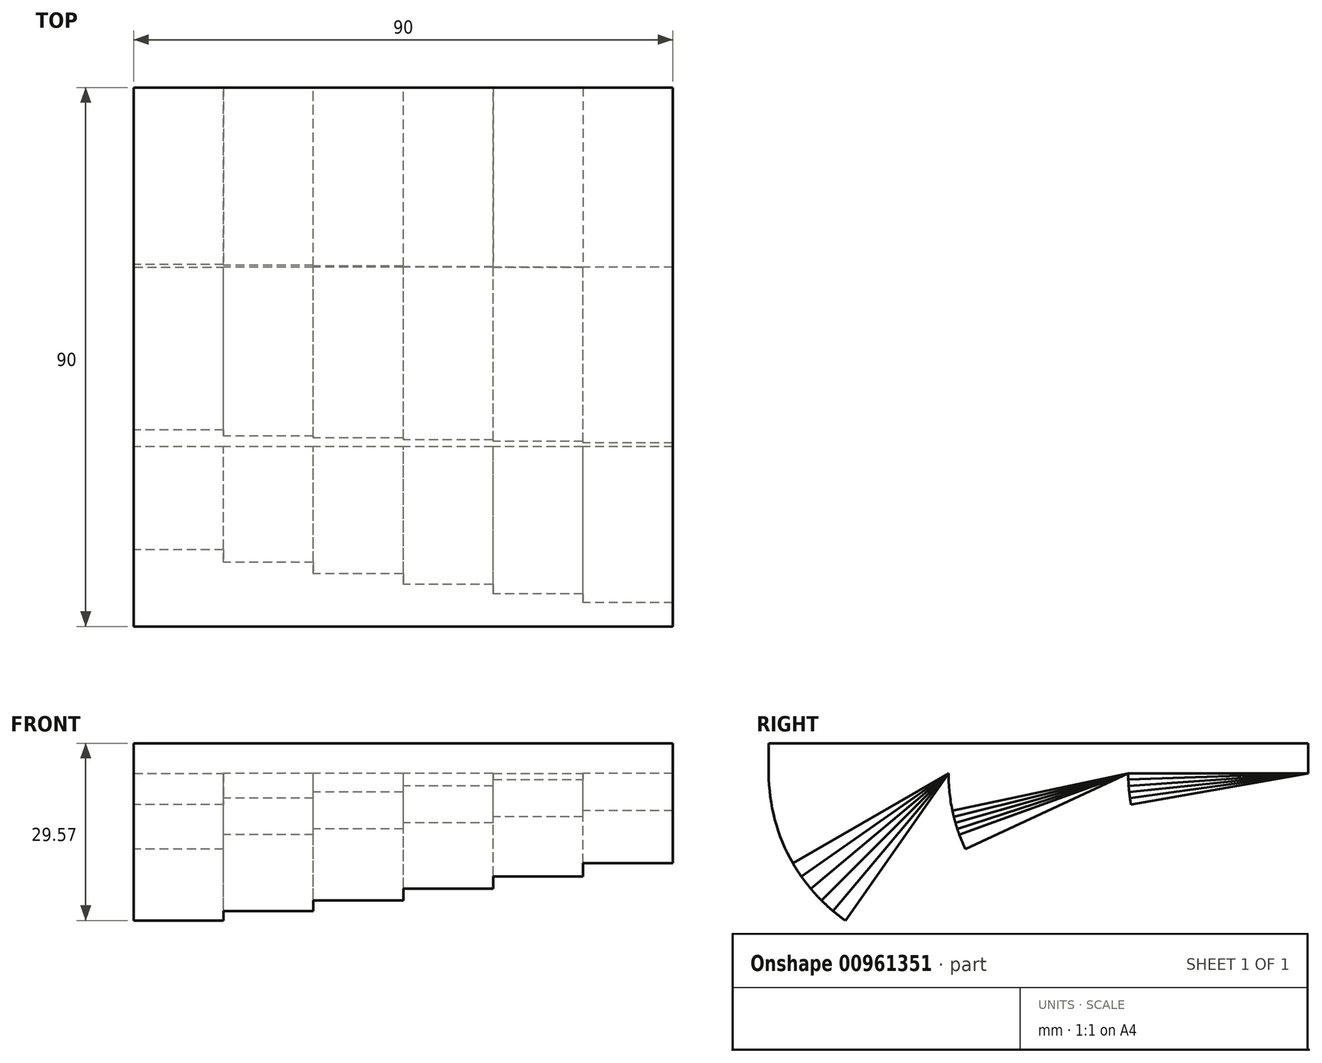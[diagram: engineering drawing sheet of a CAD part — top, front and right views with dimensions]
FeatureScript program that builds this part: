
annotation { "Feature Type Name" : "Feature", "Feature Type Description" : "" }
export const myFeature = defineFeature(function(context is Context, id is Id, definition is map)
    precondition{}
    {
        {
            var Q0;
            Q0=qCreatedBy(makeId("Top.planeOp"),FACE);
            var sketch = newSketch(context, id + "F0", { "sketchPlane" : qUnion([Q0])});
            skLineSegment(sketch, "E0.bottom", {"start": v(-45, 45) * mm, "end": v(45, 45) * mm});
            skLineSegment(sketch, "E0.top", {"start": v(-45, -45) * mm, "end": v(45, -45) * mm});
            skLineSegment(sketch, "E0.left", {"start": v(-45, -45) * mm, "end": v(-45, 45) * mm});
            skLineSegment(sketch, "E0.right", {"start": v(45, -45) * mm, "end": v(45, 45) * mm});
            skSolve(sketch);
        }
        {
            var Q0;
            Q0 = qSketchRegion(id + "F0", true);
            extrude(context, id + "F1", {"entities" : qUnion([Q0]), "depth" : 5 * mm, "offsetDistance" : 25 * mm});
        }
        {
            var Q0;
            Q0=qCreatedBy(makeId("Top.planeOp"),FACE);
            var sketch = newSketch(context, id + "F2", { "sketchPlane" : qUnion([Q0])});
            skLineSegment(sketch, "E1.bottom", {"start": v(15, 45) * mm, "end": v(30, 45) * mm});
            skLineSegment(sketch, "E1.top", {"start": v(15, 15) * mm, "end": v(30, 15) * mm});
            skLineSegment(sketch, "E1.left", {"start": v(15, 45) * mm, "end": v(15, 15) * mm});
            skLineSegment(sketch, "E1.right", {"start": v(30, 45) * mm, "end": v(30, 15) * mm});
            skSolve(sketch);
        }
        {
            var Q0;
            Q0 = qSketchRegion(id + "F2", true);
            var Q1;
            Q1=sQuery(id+"F2.wireOp",EDGE,"E1.bottom");
            revolve(context, id + "F3", {"operationType" : NewBodyOperationType.ADD, "surfaceOperationType" : NewSurfaceOperationType.NEW, "entities" : qUnion([Q0]), "axis" : qUnion([Q1]), "revolveType" : RevolveType.ONE_DIRECTION, "angle" : 2 * degree});
        }
        {
            var Q0;
            Q0=qCreatedBy(makeId("Top.planeOp"),FACE);
            var sketch = newSketch(context, id + "F4", { "sketchPlane" : qUnion([Q0])});
            skLineSegment(sketch, "E2.bottom", {"start": v(15, 15) * mm, "end": v(0, 15) * mm});
            skLineSegment(sketch, "E2.top", {"start": v(15, 45) * mm, "end": v(0, 45) * mm});
            skLineSegment(sketch, "E2.left", {"start": v(15, 15) * mm, "end": v(15, 45) * mm});
            skLineSegment(sketch, "E2.right", {"start": v(0, 15) * mm, "end": v(0, 45) * mm});
            skSolve(sketch);
        }
        {
            var Q0;
            Q0 = qSketchRegion(id + "F4", true);
            var Q1;
            Q1=sQuery(id+"F4.wireOp",EDGE,"E2.top");
            revolve(context, id + "F5", {"operationType" : NewBodyOperationType.ADD, "surfaceOperationType" : NewSurfaceOperationType.NEW, "entities" : qUnion([Q0]), "axis" : qUnion([Q1]), "revolveType" : RevolveType.ONE_DIRECTION, "oppositeDirection" : true, "angle" : 4 * degree});
        }
        {
            var Q0;
            Q0=qCreatedBy(makeId("Top.planeOp"),FACE);
            var sketch = newSketch(context, id + "F6", { "sketchPlane" : qUnion([Q0])});
            skLineSegment(sketch, "E3.bottom", {"start": v(0, 15) * mm, "end": v(-15, 15) * mm});
            skLineSegment(sketch, "E3.top", {"start": v(0, 45) * mm, "end": v(-15, 45) * mm});
            skLineSegment(sketch, "E3.left", {"start": v(0, 15) * mm, "end": v(0, 45) * mm});
            skLineSegment(sketch, "E3.right", {"start": v(-15, 15) * mm, "end": v(-15, 45) * mm});
            skSolve(sketch);
        }
        {
            var Q0;
            Q0 = qSketchRegion(id + "F6", true);
            var Q1;
            Q1=sQuery(id+"F6.wireOp",EDGE,"E3.top");
            revolve(context, id + "F7", {"operationType" : NewBodyOperationType.ADD, "surfaceOperationType" : NewSurfaceOperationType.NEW, "entities" : qUnion([Q0]), "axis" : qUnion([Q1]), "revolveType" : RevolveType.ONE_DIRECTION, "oppositeDirection" : true, "angle" : 6 * degree});
        }
        {
            var Q0;
            Q0=qCreatedBy(makeId("Top.planeOp"),FACE);
            var sketch = newSketch(context, id + "F8", { "sketchPlane" : qUnion([Q0])});
            skLineSegment(sketch, "E4.bottom", {"start": v(-15, 15) * mm, "end": v(-30, 15) * mm});
            skLineSegment(sketch, "E4.top", {"start": v(-15, 45) * mm, "end": v(-30, 45) * mm});
            skLineSegment(sketch, "E4.left", {"start": v(-15, 15) * mm, "end": v(-15, 45) * mm});
            skLineSegment(sketch, "E4.right", {"start": v(-30, 15) * mm, "end": v(-30, 45) * mm});
            skSolve(sketch);
        }
        {
            var Q0;
            Q0 = qSketchRegion(id + "F8", true);
            var Q1;
            Q1=sQuery(id+"F8.wireOp",EDGE,"E4.top");
            revolve(context, id + "F9", {"operationType" : NewBodyOperationType.ADD, "surfaceOperationType" : NewSurfaceOperationType.NEW, "entities" : qUnion([Q0]), "axis" : qUnion([Q1]), "revolveType" : RevolveType.ONE_DIRECTION, "oppositeDirection" : true, "angle" : 8 * degree});
        }
        {
            var Q0;
            Q0=qCreatedBy(makeId("Top.planeOp"),FACE);
            var sketch = newSketch(context, id + "F10", { "sketchPlane" : qUnion([Q0])});
            skLineSegment(sketch, "E5.bottom", {"start": v(-30, 45) * mm, "end": v(-45, 45) * mm});
            skLineSegment(sketch, "E5.top", {"start": v(-30, 15) * mm, "end": v(-45, 15) * mm});
            skLineSegment(sketch, "E5.left", {"start": v(-30, 45) * mm, "end": v(-30, 15) * mm});
            skLineSegment(sketch, "E5.right", {"start": v(-45, 45) * mm, "end": v(-45, 15) * mm});
            skSolve(sketch);
        }
        {
            var Q0;
            Q0 = qSketchRegion(id + "F10", true);
            var Q1;
            Q1=sQuery(id+"F10.wireOp",EDGE,"E5.bottom");
            revolve(context, id + "F11", {"operationType" : NewBodyOperationType.ADD, "surfaceOperationType" : NewSurfaceOperationType.NEW, "entities" : qUnion([Q0]), "axis" : qUnion([Q1]), "revolveType" : RevolveType.ONE_DIRECTION, "oppositeDirection" : true, "angle" : 10 * degree});
        }
        {
            var Q0;
            Q0=qCreatedBy(makeId("Top.planeOp"),FACE);
            var sketch = newSketch(context, id + "F12", { "sketchPlane" : qUnion([Q0])});
            skLineSegment(sketch, "E6.bottom", {"start": v(45, -15) * mm, "end": v(30, -15) * mm});
            skLineSegment(sketch, "E6.top", {"start": v(45, 15) * mm, "end": v(30, 15) * mm});
            skLineSegment(sketch, "E6.left", {"start": v(45, -15) * mm, "end": v(45, 15) * mm});
            skLineSegment(sketch, "E6.right", {"start": v(30, -15) * mm, "end": v(30, 15) * mm});
            skSolve(sketch);
        }
        {
            var Q0;
            Q0 = qSketchRegion(id + "F12", true);
            var Q1;
            Q1=sQuery(id+"F12.wireOp",EDGE,"E6.top");
            revolve(context, id + "F13", {"operationType" : NewBodyOperationType.ADD, "surfaceOperationType" : NewSurfaceOperationType.NEW, "entities" : qUnion([Q0]), "axis" : qUnion([Q1]), "revolveType" : RevolveType.ONE_DIRECTION, "oppositeDirection" : true, "angle" : 12 * degree});
        }
        {
            var Q0;
            Q0=qCreatedBy(makeId("Top.planeOp"),FACE);
            var sketch = newSketch(context, id + "F14", { "sketchPlane" : qUnion([Q0])});
            skLineSegment(sketch, "E7.bottom", {"start": v(30, -15) * mm, "end": v(15, -15) * mm});
            skLineSegment(sketch, "E7.top", {"start": v(30, 15) * mm, "end": v(15, 15) * mm});
            skLineSegment(sketch, "E7.left", {"start": v(30, -15) * mm, "end": v(30, 15) * mm});
            skLineSegment(sketch, "E7.right", {"start": v(15, -15) * mm, "end": v(15, 15) * mm});
            skSolve(sketch);
        }
        {
            var Q0;
            Q0 = qSketchRegion(id + "F14", true);
            var Q1;
            Q1=sQuery(id+"F14.wireOp",EDGE,"E7.top");
            revolve(context, id + "F15", {"operationType" : NewBodyOperationType.ADD, "surfaceOperationType" : NewSurfaceOperationType.NEW, "entities" : qUnion([Q0]), "axis" : qUnion([Q1]), "revolveType" : RevolveType.ONE_DIRECTION, "oppositeDirection" : true, "angle" : 14 * degree});
        }
        {
            var Q0;
            Q0=qCreatedBy(makeId("Top.planeOp"),FACE);
            var sketch = newSketch(context, id + "F16", { "sketchPlane" : qUnion([Q0])});
            skLineSegment(sketch, "E8.bottom", {"start": v(15, -15) * mm, "end": v(0, -15) * mm});
            skLineSegment(sketch, "E8.top", {"start": v(15, 15) * mm, "end": v(0, 15) * mm});
            skLineSegment(sketch, "E8.left", {"start": v(15, -15) * mm, "end": v(15, 15) * mm});
            skLineSegment(sketch, "E8.right", {"start": v(0, -15) * mm, "end": v(0, 15) * mm});
            skSolve(sketch);
        }
        {
            var Q0;
            Q0 = qSketchRegion(id + "F16", true);
            var Q1;
            Q1=sQuery(id+"F16.wireOp",EDGE,"E8.top");
            revolve(context, id + "F17", {"operationType" : NewBodyOperationType.ADD, "surfaceOperationType" : NewSurfaceOperationType.NEW, "entities" : qUnion([Q0]), "axis" : qUnion([Q1]), "revolveType" : RevolveType.ONE_DIRECTION, "oppositeDirection" : true, "angle" : 16 * degree});
        }
        {
            var Q0;
            Q0=qCreatedBy(makeId("Top.planeOp"),FACE);
            var sketch = newSketch(context, id + "F18", { "sketchPlane" : qUnion([Q0])});
            skLineSegment(sketch, "E9.bottom", {"start": v(0, -15) * mm, "end": v(-15, -15) * mm});
            skLineSegment(sketch, "E9.top", {"start": v(0, 15) * mm, "end": v(-15, 15) * mm});
            skLineSegment(sketch, "E9.left", {"start": v(0, -15) * mm, "end": v(0, 15) * mm});
            skLineSegment(sketch, "E9.right", {"start": v(-15, -15) * mm, "end": v(-15, 15) * mm});
            skSolve(sketch);
        }
        {
            var Q0;
            Q0 = qSketchRegion(id + "F18", true);
            var Q1;
            Q1=sQuery(id+"F6.wireOp",EDGE,"E3.bottom");
            revolve(context, id + "F19", {"operationType" : NewBodyOperationType.ADD, "surfaceOperationType" : NewSurfaceOperationType.NEW, "entities" : qUnion([Q0]), "axis" : qUnion([Q1]), "revolveType" : RevolveType.ONE_DIRECTION, "oppositeDirection" : true, "angle" : 18 * degree});
        }
        {
            var Q0;
            Q0=qCreatedBy(makeId("Top.planeOp"),FACE);
            var sketch = newSketch(context, id + "F20", { "sketchPlane" : qUnion([Q0])});
            skLineSegment(sketch, "E10.bottom", {"start": v(-15, -15) * mm, "end": v(-30, -15) * mm});
            skLineSegment(sketch, "E10.top", {"start": v(-15, 15) * mm, "end": v(-30, 15) * mm});
            skLineSegment(sketch, "E10.left", {"start": v(-15, -15) * mm, "end": v(-15, 15) * mm});
            skLineSegment(sketch, "E10.right", {"start": v(-30, -15) * mm, "end": v(-30, 15) * mm});
            skSolve(sketch);
        }
        {
            var Q0;
            Q0 = qSketchRegion(id + "F20", true);
            var Q1;
            Q1=sQuery(id+"F20.wireOp",EDGE,"E10.top");
            revolve(context, id + "F21", {"operationType" : NewBodyOperationType.ADD, "surfaceOperationType" : NewSurfaceOperationType.NEW, "entities" : qUnion([Q0]), "axis" : qUnion([Q1]), "revolveType" : RevolveType.ONE_DIRECTION, "oppositeDirection" : true, "angle" : 20 * degree});
        }
        {
            var Q0;
            Q0=qCreatedBy(makeId("Top.planeOp"),FACE);
            var sketch = newSketch(context, id + "F22", { "sketchPlane" : qUnion([Q0])});
            skLineSegment(sketch, "E11.bottom", {"start": v(-30, -15) * mm, "end": v(-45, -15) * mm});
            skLineSegment(sketch, "E11.top", {"start": v(-30, 15) * mm, "end": v(-45, 15) * mm});
            skLineSegment(sketch, "E11.left", {"start": v(-30, -15) * mm, "end": v(-30, 15) * mm});
            skLineSegment(sketch, "E11.right", {"start": v(-45, -15) * mm, "end": v(-45, 15) * mm});
            skSolve(sketch);
        }
        {
            var Q0;
            Q0 = qSketchRegion(id + "F22", true);
            var Q1;
            Q1=sQuery(id+"F22.wireOp",EDGE,"E11.top");
            revolve(context, id + "F23", {"operationType" : NewBodyOperationType.ADD, "surfaceOperationType" : NewSurfaceOperationType.NEW, "entities" : qUnion([Q0]), "axis" : qUnion([Q1]), "revolveType" : RevolveType.ONE_DIRECTION, "oppositeDirection" : true, "angle" : 25 * degree});
        }
        {
            var Q0;
            Q0=qCreatedBy(makeId("Top.planeOp"),FACE);
            var sketch = newSketch(context, id + "F24", { "sketchPlane" : qUnion([Q0])});
            skLineSegment(sketch, "E12.bottom", {"start": v(45, -45) * mm, "end": v(30, -45) * mm});
            skLineSegment(sketch, "E12.top", {"start": v(45, -15) * mm, "end": v(30, -15) * mm});
            skLineSegment(sketch, "E12.left", {"start": v(45, -45) * mm, "end": v(45, -15) * mm});
            skLineSegment(sketch, "E12.right", {"start": v(30, -45) * mm, "end": v(30, -15) * mm});
            skSolve(sketch);
        }
        {
            var Q0;
            Q0 = qSketchRegion(id + "F24", true);
            var Q1;
            Q1=sQuery(id+"F24.wireOp",EDGE,"E12.top");
            revolve(context, id + "F25", {"operationType" : NewBodyOperationType.ADD, "surfaceOperationType" : NewSurfaceOperationType.NEW, "entities" : qUnion([Q0]), "axis" : qUnion([Q1]), "revolveType" : RevolveType.ONE_DIRECTION, "oppositeDirection" : true, "angle" : 30 * degree});
        }
        {
            var Q0;
            Q0=qCreatedBy(makeId("Top.planeOp"),FACE);
            var sketch = newSketch(context, id + "F26", { "sketchPlane" : qUnion([Q0])});
            skLineSegment(sketch, "E13.bottom", {"start": v(30, -45) * mm, "end": v(15, -45) * mm});
            skLineSegment(sketch, "E13.top", {"start": v(30, -15) * mm, "end": v(15, -15) * mm});
            skLineSegment(sketch, "E13.left", {"start": v(30, -45) * mm, "end": v(30, -15) * mm});
            skLineSegment(sketch, "E13.right", {"start": v(15, -45) * mm, "end": v(15, -15) * mm});
            skSolve(sketch);
        }
        {
            var Q0;
            Q0 = qSketchRegion(id + "F26", true);
            var Q1;
            Q1=sQuery(id+"F26.wireOp",EDGE,"E13.top");
            revolve(context, id + "F27", {"operationType" : NewBodyOperationType.ADD, "surfaceOperationType" : NewSurfaceOperationType.NEW, "entities" : qUnion([Q0]), "axis" : qUnion([Q1]), "revolveType" : RevolveType.ONE_DIRECTION, "oppositeDirection" : true, "angle" : 35 * degree});
        }
        {
            var Q0;
            Q0=qCreatedBy(makeId("Top.planeOp"),FACE);
            var sketch = newSketch(context, id + "F28", { "sketchPlane" : qUnion([Q0])});
            skLineSegment(sketch, "E14.bottom", {"start": v(15, -45) * mm, "end": v(0, -45) * mm});
            skLineSegment(sketch, "E14.top", {"start": v(15, -15) * mm, "end": v(0, -15) * mm});
            skLineSegment(sketch, "E14.left", {"start": v(15, -45) * mm, "end": v(15, -15) * mm});
            skLineSegment(sketch, "E14.right", {"start": v(0, -45) * mm, "end": v(0, -15) * mm});
            skSolve(sketch);
        }
        {
            var Q0;
            Q0 = qSketchRegion(id + "F28", true);
            var Q1;
            Q1=sQuery(id+"F16.wireOp",EDGE,"E8.bottom");
            revolve(context, id + "F29", {"operationType" : NewBodyOperationType.ADD, "surfaceOperationType" : NewSurfaceOperationType.NEW, "entities" : qUnion([Q0]), "axis" : qUnion([Q1]), "revolveType" : RevolveType.ONE_DIRECTION, "oppositeDirection" : true, "angle" : 40 * degree});
        }
        {
            var Q0;
            Q0=qCreatedBy(makeId("Top.planeOp"),FACE);
            var sketch = newSketch(context, id + "F30", { "sketchPlane" : qUnion([Q0])});
            skLineSegment(sketch, "E15.bottom", {"start": v(0, -45) * mm, "end": v(-15, -45) * mm});
            skLineSegment(sketch, "E15.top", {"start": v(0, -15) * mm, "end": v(-15, -15) * mm});
            skLineSegment(sketch, "E15.left", {"start": v(0, -45) * mm, "end": v(0, -15) * mm});
            skLineSegment(sketch, "E15.right", {"start": v(-15, -45) * mm, "end": v(-15, -15) * mm});
            skSolve(sketch);
        }
        {
            var Q0;
            Q0 = qSketchRegion(id + "F30", true);
            var Q1;
            Q1=sQuery(id+"F30.wireOp",EDGE,"E15.top");
            revolve(context, id + "F31", {"operationType" : NewBodyOperationType.ADD, "surfaceOperationType" : NewSurfaceOperationType.NEW, "entities" : qUnion([Q0]), "axis" : qUnion([Q1]), "revolveType" : RevolveType.ONE_DIRECTION, "oppositeDirection" : true, "angle" : 45 * degree});
        }
        {
            var Q0;
            Q0=qCreatedBy(makeId("Top.planeOp"),FACE);
            var sketch = newSketch(context, id + "F32", { "sketchPlane" : qUnion([Q0])});
            skLineSegment(sketch, "E16.bottom", {"start": v(-15, -45) * mm, "end": v(-30, -45) * mm});
            skLineSegment(sketch, "E16.top", {"start": v(-15, -15) * mm, "end": v(-30, -15) * mm});
            skLineSegment(sketch, "E16.left", {"start": v(-15, -45) * mm, "end": v(-15, -15) * mm});
            skLineSegment(sketch, "E16.right", {"start": v(-30, -45) * mm, "end": v(-30, -15) * mm});
            skSolve(sketch);
        }
        {
            var Q0;
            Q0 = qSketchRegion(id + "F32", true);
            var Q1;
            Q1=sQuery(id+"F32.wireOp",EDGE,"E16.top");
            revolve(context, id + "F33", {"operationType" : NewBodyOperationType.ADD, "surfaceOperationType" : NewSurfaceOperationType.NEW, "entities" : qUnion([Q0]), "axis" : qUnion([Q1]), "revolveType" : RevolveType.ONE_DIRECTION, "oppositeDirection" : true, "angle" : 50 * degree});
        }
        {
            var Q0;
            Q0=qCreatedBy(makeId("Top.planeOp"),FACE);
            var sketch = newSketch(context, id + "F34", { "sketchPlane" : qUnion([Q0])});
            skLineSegment(sketch, "E17.bottom", {"start": v(-30, -45) * mm, "end": v(-45, -45) * mm});
            skLineSegment(sketch, "E17.top", {"start": v(-30, -15) * mm, "end": v(-45, -15) * mm});
            skLineSegment(sketch, "E17.left", {"start": v(-30, -45) * mm, "end": v(-30, -15) * mm});
            skLineSegment(sketch, "E17.right", {"start": v(-45, -45) * mm, "end": v(-45, -15) * mm});
            skSolve(sketch);
        }
        {
            var Q0;
            Q0 = qSketchRegion(id + "F34", true);
            var Q1;
            Q1=sQuery(id+"F34.wireOp",EDGE,"E17.top");
            revolve(context, id + "F35", {"operationType" : NewBodyOperationType.ADD, "surfaceOperationType" : NewSurfaceOperationType.NEW, "entities" : qUnion([Q0]), "axis" : qUnion([Q1]), "revolveType" : RevolveType.ONE_DIRECTION, "oppositeDirection" : true, "angle" : 55 * degree});
        }
    });
